# Revit family: Zumtobel CRAFT LED
name_source: partatom
category: Lighting Fixtures
revit_build: Autodesk Revit 2014 (Build: 20130308_1515(x64)
units: mm (PartAtom-declared; Revit-internal decimal feet)

## types (19) — shared parameters
Adaptor Length = 613 mm  [stored 2.01115 ft]
Assembly Code = D5020200
Color Filter = 16777215
Dimming Lamp Color Temperature Shift = <None>
Emit Shape Visible in Rendering = No
Lamp = LED
Manufacturer = Zumtobel Lighting
Tilt Angle = -90.00°
URL = http://www.zumtobel.com
Voltage = 230 V
zero-valued in all types: Default Elevation

## per-type parameters (varying)
| type | 331 Length | 657 Length | Apparent Load | Craft M L | Craft S | Description | Emit from Rectangle Length | Emit from Rectangle Width | FI Cover | Height | Length | Model | PST | Photometric Web File | Width |
| CRAFT L - NB | No | Yes | 196 VA | Yes | No | LED high-bay luminaire - large | 657 mm | 332.38 mm  [stored 1.09049 ft] | No | 125 mm  [stored 0.410105 ft] | 657 mm | 42182795 | No | D34747AA_CRAFT_LED26000-840_L660_PC_NB.IES | 330 mm |
| CRAFT L - WB | No | Yes | 196 VA | Yes | No | LED high-bay luminaire - large | 657 mm | 332.38 mm  [stored 1.09049 ft] | No | 125 mm  [stored 0.410105 ft] | 657 mm | 42182668 | No | D34498AA_CRAFT_LED26000-840_L660_PC_WB.IES | 330 mm |
| CRAFT L TEC - WB | No | Yes | 196 VA | Yes | No | LED high-bay luminaire - large | 657 mm | 332.38 mm  [stored 1.09049 ft] | No | 125 mm  [stored 0.410105 ft] | 657 mm | 42183587 | No | D34498AA_CRAFT_LED26000-840_L660_PC_WB.IES | 330 mm |
| CRAFT L  FI - WB | No | Yes | 184 VA | Yes | No | LED high-bay luminaire - large | 657 mm | 332.38 mm  [stored 1.09049 ft] | Yes | 125 mm  [stored 0.410105 ft] | 657 mm | 42182495 | No | D34498AA_CRAFT_FI_LED25000-840_L660_PC_WB.IES | 330 mm |
| CRAFT L  PST - NB | No | Yes | 196 VA | Yes | No | LED high-bay luminaire - large | 657 mm | 332.38 mm  [stored 1.09049 ft] | Yes | 125 mm  [stored 0.410105 ft] | 657 mm | 42183075 | Yes | D34747AA_CRAFT_LED26000-840_L660_PC_NB.IES | 330 mm |
| CRAFT L  PST - WB | No | Yes | 196 VA | Yes | No | LED high-bay luminaire - large | 657 mm | 332.38 mm  [stored 1.09049 ft] | Yes | 125 mm  [stored 0.410105 ft] | 657 mm | 42183033 | Yes | D34498AA_CRAFT_LED26000-840_L660_PC_WB.IES | 330 mm |
| CRAFT M  PST - WB | Yes | No | 98 VA | Yes | No | LED high-bay luminaire - medium | 331 mm  [stored 1.08596 ft] | 333.38 mm  [stored 1.09377 ft] | No | 170 mm  [stored 0.557743 ft] | 331 mm  [stored 1.08596 ft] | 42183031 | Yes | D34498AA_CRAFT_LED13000-840_L330_PC_WB.IES | 331 mm  [stored 1.08596 ft] |
| CRAFT M  PST - NB | Yes | No | 98 VA | Yes | No | LED high-bay luminaire - medium | 331 mm  [stored 1.08596 ft] | 333.38 mm  [stored 1.09377 ft] | No | 170 mm  [stored 0.557743 ft] | 331 mm  [stored 1.08596 ft] | 42183073 | Yes | D34747AA_CRAFT_LED13000-840_L330_PC_NB.IES | 331 mm  [stored 1.08596 ft] |
| CRAFT M FI - WB | Yes | No | 92 VA | Yes | No | LED high-bay luminaire - medium | 331 mm  [stored 1.08596 ft] | 333.38 mm  [stored 1.09377 ft] | Yes | 125 mm  [stored 0.410105 ft] | 331 mm  [stored 1.08596 ft] | 42182494 | No | D34498AA_CRAFT_FI_LED13000-840_L330_PC_WB.IES | 331 mm  [stored 1.08596 ft] |
| CRAFT M TEC - WB | Yes | No | 98 VA | Yes | No | LED high-bay luminaire - medium | 331 mm  [stored 1.08596 ft] | 333.38 mm  [stored 1.09377 ft] | No | 125 mm  [stored 0.410105 ft] | 331 mm  [stored 1.08596 ft] | 42182667 | No | D34498AA_CRAFT_LED13000-840_L330_PC_WB.IES | 331 mm  [stored 1.08596 ft] |
| CRAFT M - WB | Yes | No | 98 VA | Yes | No | LED high-bay luminaire - medium | 331 mm  [stored 1.08596 ft] | 333.38 mm  [stored 1.09377 ft] | No | 125 mm  [stored 0.410105 ft] | 331 mm  [stored 1.08596 ft] | 42182667 | No | D34498AA_CRAFT_LED13000-840_L330_PC_WB.IES | 331 mm  [stored 1.08596 ft] |
| CRAFT M - NB | Yes | No | 98 VA | Yes | No | LED high-bay luminaire - medium | 331 mm  [stored 1.08596 ft] | 333.38 mm  [stored 1.09377 ft] | No | 125 mm  [stored 0.410105 ft] | 331 mm  [stored 1.08596 ft] | 42182793 | No | D34747AA_CRAFT_LED13000-840_L330_PC_NB.IES | 331 mm  [stored 1.08596 ft] |
| CRAFT S - NB | No | No | 65 VA | No | Yes | LED high-bay luminaire - small | 339 mm  [stored 1.1122 ft] | 167.38 mm  [stored 0.549147 ft] | No | 159 mm  [stored 0.521654 ft] | 339 mm  [stored 1.1122 ft] | 42183268 | No | D34746AA_CRAFT_LED7500-840_L330_PM_NB.IES | 165 mm |
| CRAFT L PST - WB | No | Yes | 196 VA | Yes | No | LED high-bay luminaire - large | 657 mm | 332.38 mm  [stored 1.09049 ft] | Yes | 170 mm  [stored 0.557743 ft] | 657 mm | 42183033 | Yes | D34498AA_CRAFT_LED26000-840_L660_PC_WB.IES | 330 mm |
| CRAFT L PST - NB | No | Yes | 196 VA | Yes | No | LED high-bay luminaire - large | 657 mm | 332.38 mm  [stored 1.09049 ft] | Yes | 170 mm  [stored 0.557743 ft] | 657 mm | 42183075 | Yes | D34747AA_CRAFT_LED26000-840_L660_PC_NB.IES | 330 mm |
| CRAFT L FI - WB | No | Yes | 184 VA | Yes | No | LED high-bay luminaire - large | 657 mm | 332.38 mm  [stored 1.09049 ft] | Yes | 125 mm  [stored 0.410105 ft] | 657 mm | 42182495 | No | D34498AA_CRAFT_FI_LED25000-840_L660_PC_WB.IES | 330 mm |
| CRAFT S TEC - WB | No | No | 65 VA | No | Yes | LED high-bay luminaire - small | 339 mm  [stored 1.1122 ft] | 167.38 mm  [stored 0.549147 ft] | No | 159 mm  [stored 0.521654 ft] | 339 mm  [stored 1.1122 ft] | 42183265 | No | D34741AA_CRAFT_LED7500-840_L330_PM_WB.IES | 165 mm |
| CRAFT S TEC - NB | No | No | 65 VA | No | Yes | LED high-bay luminaire - small | 339 mm  [stored 1.1122 ft] | 167.38 mm  [stored 0.549147 ft] | No | 159 mm  [stored 0.521654 ft] | 339 mm  [stored 1.1122 ft] | 42183271 | No | D34746AA_CRAFT_LED7500-840_L330_PM_NB.IES | 165 mm |
| CRAFT S - WB | No | No | 65 VA | No | Yes | LED high-bay luminaire - small | 339 mm  [stored 1.1122 ft] | 167.38 mm  [stored 0.549147 ft] | No | 159 mm  [stored 0.521654 ft] | 339 mm  [stored 1.1122 ft] | 42183262 | No | D34741AA_CRAFT_LED7500-840_L330_PM_WB.IES | 165 mm |

note: [stored X ft] marks values corroborated as IEEE doubles in the binary element streams (Revit-internal decimal feet)

## geometry (parser evidence)
native form markers: Sweep x8
no freeform markers — native parametric forms only
